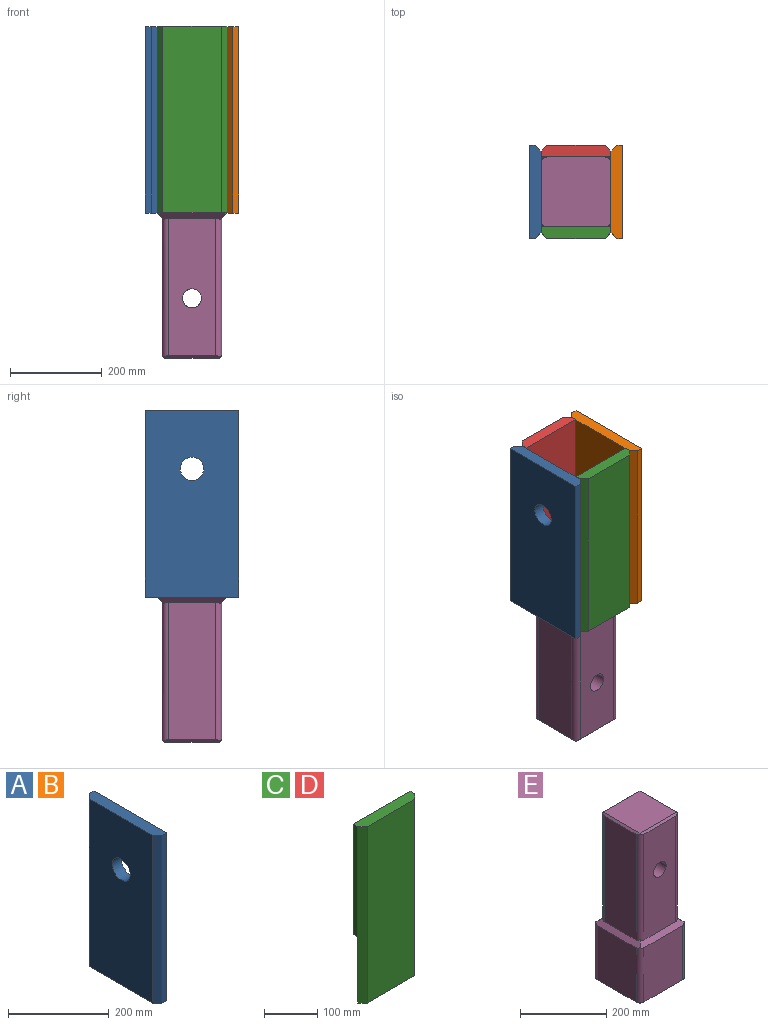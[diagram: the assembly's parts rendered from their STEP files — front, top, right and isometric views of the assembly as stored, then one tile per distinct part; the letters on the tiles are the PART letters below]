
ASSEMBLY  parts=5 mates=4
PART A: 9 faces, bbox 25.4x203.2x406.4 mm
  f0: plane 203.2x25.4mm, normal (0,0,-1), area 5000mm2, adj f1,f3,f4,f5,f7,f8
  f1: plane 406.4x12.7mm, normal (0,1,0), area 5161.3mm2, adj f0,f2,f4,f8
  f2: plane 203.2x25.4mm, normal (0,0,1), area 5000mm2, adj f1,f3,f4,f5,f7,f8
  f3: plane 406.4x12.7mm, normal (0,-1,0), area 5161.3mm2, adj f0,f2,f4,f7
  f4: plane 406.4x203.2mm, normal (1,0,0), area 80553.7mm2, adj f0,f1,f2,f3,f6
  f5: plane 406.4x177.8mm, normal (-1,0,0), area 70231.1mm2, adj f0,f2,f6,f7,f8
  f6: cylinder r=25.4mm len=50.8mm, axis (1,0,0), area 4053.7mm2, adj f4,f5
  f7: plane 406.4x12.7mm, normal (-0.71,-0.71,0), area 7299.2mm2, adj f0,f2,f3,f5
  f8: plane 406.4x12.7mm, normal (-0.71,0.71,0), area 7299.2mm2, adj f0,f1,f2,f5
PART B: same geometry as A
PART C: 12 faces, bbox 152.4x25.4x406.4 mm
  f0: plane 152.4x25.4mm, normal (0,0,-1), area 3548.4mm2, adj f4,f5,f6,f7,f8,f10
  f1: plane 254x12.7mm, normal (1,0,0), area 3225.8mm2, adj f2,f5,f6,f11
  f2: plane 152.4x25.4mm, normal (0,0,1), area 3709.7mm2, adj f1,f3,f4,f5,f6,f7
  f3: plane 254x12.7mm, normal (-1,0,0), area 3225.8mm2, adj f2,f5,f7,f9
  f4: plane 406.4x127mm, normal (0,-1,0), area 51612.8mm2, adj f0,f2,f6,f7
  f5: plane 406.4x152.4mm, normal (0,1,0), area 58064.4mm2, adj f0,f1,f2,f3,f8,f9,f10,f11
  f6: plane 406.4x12.7mm, normal (0.71,-0.71,0), area 7299.2mm2, adj f0,f1,f2,f4,f10
  f7: plane 406.4x12.7mm, normal (-0.71,-0.71,0), area 7299.2mm2, adj f0,f2,f3,f4,f8
  f8: plane 152.4x12.7mm, normal (-0.71,0.71,0), area 2737.2mm2, adj f0,f5,f7,f9
  f9: plane 12.7x12.7mm, normal (0,0,-1), area 80.6mm2, adj f3,f5,f8
  f10: plane 152.4x12.7mm, normal (0.71,0.71,0), area 2737.2mm2, adj f0,f5,f6,f11
  f11: plane 12.7x12.7mm, normal (0,0,-1), area 80.6mm2, adj f1,f5,f10
PART D: same geometry as C
PART E: 27 faces, bbox 152.4x152.4x469.9 mm
  f0: plane 153.82x127mm, normal (0,-1,0), area 19535.4mm2, adj f4,f11,f23,f26
  f1: plane 153.82x127mm, normal (1,0,0), area 19535.4mm2, adj f4,f12,f23,f24
  f2: plane 153.82x127mm, normal (0,1,0), area 19535.4mm2, adj f4,f14,f24,f25
  f3: plane 153.82x127mm, normal (-1,0,0), area 19535.4mm2, adj f4,f13,f25,f26
  f4: plane 152.4x152.4mm, normal (0,0,-1), area 23087.3mm2, adj f0,f1,f2,f3,f23,f24,f25,f26
  f5: plane 299.72x104.45mm, normal (0,-1,0), area 29966.2mm2, adj f10,f11,f16,f19,f22
  f6: plane 299.72x104.45mm, normal (1,0,0), area 31304.2mm2, adj f12,f18,f21,f22
  f7: plane 299.72x104.45mm, normal (0,1,0), area 29966.2mm2, adj f10,f14,f17,f20,f21
  f8: plane 299.72x104.45mm, normal (-1,0,0), area 31304.2mm2, adj f13,f15,f19,f20
  f9: plane 119.69x119.69mm, normal (0,0,1), area 14324.5mm2, adj f15,f16,f17,f18
  f10: cylinder r=20.64mm len=129.84mm, axis (0,1,0), area 16836.9mm2, adj f5,f7
  f11: plane 144.96x15mm, normal (0,-0.71,0.71), area 2250.8mm2, adj f0,f5,f12,f13,f19,f22,f23,f26
  f12: plane 144.96x15mm, normal (0.71,0,0.71), area 2250.8mm2, adj f1,f6,f11,f14,f21,f22,f23,f24
  f13: plane 144.96x15mm, normal (-0.71,0,0.71), area 2250.8mm2, adj f3,f8,f11,f14,f19,f20,f25,f26
  f14: plane 144.96x15mm, normal (0,0.71,0.71), area 2250.8mm2, adj f2,f7,f12,f13,f20,f21,f24,f25
  f15: plane 122.41x5.08mm, normal (-0.71,0,0.71), area 847.4mm2, adj f8,f9,f16,f17,f19,f20
  f16: plane 122.41x5.08mm, normal (0,-0.71,0.71), area 847.4mm2, adj f5,f9,f15,f18,f19,f22
  f17: plane 122.41x5.08mm, normal (0,0.71,0.71), area 847.4mm2, adj f7,f9,f15,f18,f20,f21
  f18: plane 122.41x5.08mm, normal (0.71,0,0.71), area 847.4mm2, adj f6,f9,f16,f17,f21,f22
  f19: cylinder r=12.7mm len=303.44mm, axis (0,0,-1), area 5979.1mm2, adj f5,f8,f11,f13,f15,f16
  f20: cylinder r=12.7mm len=303.44mm, axis (0,0,1), area 5979.1mm2, adj f7,f8,f13,f14,f15,f17
  f21: cylinder r=12.7mm len=303.44mm, axis (0,0,-1), area 5979.1mm2, adj f6,f7,f12,f14,f17,f18
  f22: cylinder r=12.7mm len=303.44mm, axis (0,0,1), area 5979.1mm2, adj f5,f6,f11,f12,f16,f18
  f23: cylinder r=12.7mm len=157.54mm, axis (0,0,1), area 3093.9mm2, adj f0,f1,f4,f11,f12
  f24: cylinder r=12.7mm len=157.54mm, axis (0,0,-1), area 3093.9mm2, adj f1,f2,f4,f12,f14
  f25: cylinder r=12.7mm len=157.54mm, axis (0,0,1), area 3093.9mm2, adj f2,f3,f4,f13,f14
  f26: cylinder r=12.7mm len=157.54mm, axis (0,0,-1), area 3093.9mm2, adj f0,f3,f4,f11,f13
PLACE A rot(axis=(0,0,1),180deg) t=(-377.03,-47.21,133.71)mm
PLACE B rot(axis=(0,1,0),0deg) t=(-224.63,-47.21,133.71)mm
PLACE C rot(axis=(0.2,0.97,0.14),0deg) t=(-300.83,-123.41,135.13)mm
PLACE D rot(axis=(0,0,1),180deg) t=(-300.83,28.99,135.13)mm
PLACE E rot(axis=(0,-1,0),180deg) t=(-300.83,-47.21,84.33)mm
MATE fastened B.f5 <-> E.f3  axis (-1,0,0) through (-224.63,-47.21,-69.49)mm
MATE fastened C.f5 <-> E.f0  axis (0,1,0) through (-300.83,-123.41,-68.07)mm
MATE fastened A.f5 <-> E.f1  axis (1,0,0) through (-377.03,-47.21,-69.49)mm
MATE fastened D.f5 <-> E.f2  axis (0,-1,0) through (-300.83,28.99,-68.07)mm
